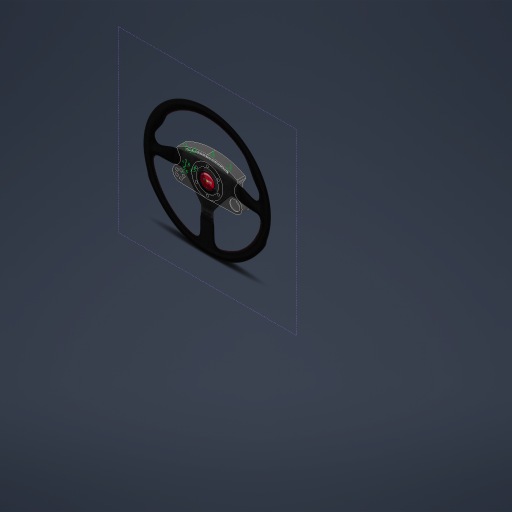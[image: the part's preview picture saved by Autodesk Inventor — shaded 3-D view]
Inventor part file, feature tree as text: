
AUTODESK INVENTOR PART (.ipt)
format: ipt  version: 2023 (Build 270158000, 158)  size: 2,766,848 bytes
history: native  units: mm
features: extrude x19, sketch x13, fillet x9, projected_geometry x6, other x3, chamfer x2, split x1, mirror x1, plane x1
ambient origin geometry x8: Origin, YZ Plane, XZ Plane, XY Plane, X Axis, Y Axis, Z Axis, Center Point
bodies: Solid1 (feature_tree)
feature tree (55):
  sketch  "Sketch1"  dims[d5=61.0mm d6=70.0mm]
  extrude  "Extrusion1"  Depth=70.0mm
  extrude  "Extrusion2"  Depth=60.0mm TaperAngle=360.0deg
  split  "Split1"
  sketch  "Sketch4"  dims[d14=86.0mm d36=20.0mm d37=0.0mm]
  sketch  "Sketch5"  dims[d38=40.0mm d49=75.888542mm]
  extrude  "Extrusion3"  Depth=20.0mm TaperAngle=0.0deg
  extrude  "Extrusion4"  Depth=75.888542mm
  extrude  "Extrusion5"  Depth=20.383104mm
  extrude  "Extrusion6"  Depth=28.0mm
  extrude  "Extrusion8"  Depth=10.458mm
  extrude  "Extrusion20"  Depth=50.0mm TaperAngle=360.0deg
  sketch  "Sketch7"  dims[d50=75.888542mm d51=20.383104mm]
  extrude  "Extrusion9"  Depth=10.0mm TaperAngle=360.0deg
  extrude  "Extrusion10"  Depth=13.5mm TaperAngle=0.0deg
  mirror  "Mirror1"
  extrude  "Extrusion11"  Depth=5.5mm
  extrude  "Extrusion12"  Depth=50.0mm TaperAngle=360.0deg
  chamfer  "Chamfer3"  Distance=13.5mm
  fillet  "Fillet1"  [1 undecoded]
  plane  "Work Plane4"
  sketch  "Sketch11"  dims[d54=1.5mm d55=0.0mm d61=10.458mm]
  sketch  "Sketch12"  dims[d62=8.0mm d63=50.0mm d65=360.0deg]
  extrude  "Extrusion14"  Depth=17.0mm
  extrude  "Extrusion19"  Depth=17.0mm
  extrude  "Extrusion15"  TaperAngle=90.0deg  [1 undecoded]
  fillet  "Fillet2"  Radius=2.0mm
  fillet  "Fillet3"  Radius=8.0mm
  extrude  "Extrusion16"  Depth=3.0mm TaperAngle=0.0deg
  sketch  "Sketch15"  dims[d77=5.0mm d78=0.0mm d82=5.5mm]
  extrude  "Extrusion17"  Depth=17.0mm
  extrude  "Extrusion18"  Depth=17.0mm
  fillet  "Fillet4"  Radius=3.5mm
  fillet  "Fillet5"  Radius=20.0mm
  fillet  "Fillet6"  Radius=20.0mm
  fillet  "Fillet7"  Radius=5.0mm
  fillet  "Fillet9"  Radius=5.0mm
  chamfer  "Chamfer6"  Distance=80.0mm
  sketch  "Sketch17"  dims[d83=1.0mm d84=50.0mm d86=360.0deg d88=13.5mm d89=0.0mm d92=0.0mm d93=0.0mm]
  fillet  "Fillet11"  Radius=2.0mm
  extrude  "Extrusion21"  Depth=17.0mm TaperAngle=45.0deg
  other  "Image1"
  other  "Image2"
  sketch  "Sketch2"  dims[d7=6.5mm d9=60.0mm d11=360.0deg]
  sketch  "Sketch8"  dims[d52=20.383104mm d53=28.0mm]
  sketch  "Sketch13"  dims[d67=10.0mm d68=50.0mm d70=360.0deg]
  sketch  "Sketch14"  dims[d72=0.0mm d73=0.0mm d74=13.5mm d75=0.0mm]
  projected_geometry  "Projected Loop4"
  projected_geometry  "Projected Loop5"
  projected_geometry  "Projected Loop6"
  projected_geometry  "Projected Loop7"
  projected_geometry  "Projected Loop8"
  projected_geometry  "Projected Loop9"
  other  "Image5"
  sketch  "Sketch18"  dims[d94=23.0mm d95=7.0mm d96=5.0mm d97=90.0deg d101=2.0mm d103=8.0mm d104=0.0mm d105=3.0mm d106=0.0mm d107=5.0mm d108=5.0mm d109=3.5mm d110=0.0mm d116=20.0mm d119=20.0mm d120=5.0mm d121=5.0mm d129=80.0mm d131=3.51199mm d148=2.0mm d149=0.0mm d154=1.5mm d155=2.0mm d156=45.0deg d164=7.0mm d165=1.0mm d166=50.0mm d168=360.0deg d170=0.0mm d242=1.0mm d243=1.0mm d244=1.0mm d245=1.0mm d246=1.0mm d247=1.0mm d248=1.0mm d249=1.0mm d250=1.0mm d251=1.0mm d252=1.0mm d253=1.0mm d254=1.0mm d255=1.0mm d256=1.0mm d257=1.0mm d258=1.0mm d259=1.0mm d260=1.0mm d261=1.0mm d262=1.0mm d263=1.0mm d264=1.0mm d265=1.0mm d266=1.0mm d267=1.0mm d268=1.0mm d269=1.0mm d270=1.0mm d271=1.0mm d272=1.0mm d273=1.0mm d274=1.0mm d275=1.0mm d276=1.0mm d277=1.0mm d278=1.0mm d279=1.0mm d280=1.0mm d281=1.0mm d282=1.0mm d283=1.0mm d284=1.0mm d285=1.0mm d286=1.0mm d287=1.0mm d288=1.0mm d289=1.0mm d290=1.0mm d291=1.0mm d292=1.0mm d293=1.0mm d294=1.0mm d295=1.0mm d296=1.0mm d297=1.0mm d298=1.0mm d299=1.0mm d300=1.0mm d301=1.0mm d302=1.0mm d303=1.0mm d304=1.0mm d305=1.0mm d306=1.0mm d307=1.0mm d308=1.0mm d309=1.0mm d310=1.0mm d311=1.0mm d312=1.0mm d313=1.0mm d314=1.0mm d315=1.0mm d316=1.0mm d317=1.0mm d318=1.0mm d319=1.0mm d320=1.0mm d321=1.0mm d322=1.0mm d323=1.0mm d324=1.0mm d325=1.0mm d326=1.0mm d327=1.0mm d328=1.0mm d329=1.0mm d330=1.0mm d331=1.0mm d332=1.0mm d333=1.0mm d334=1.0mm d335=1.0mm d336=1.0mm d337=1.0mm d338=1.0mm d339=1.0mm d340=1.0mm d341=1.0mm d342=1.0mm d343=1.0mm d344=1.0mm d345=1.0mm d348=10.5mm d349=0.0mm d350=5.0mm d351=8.061767mm d373=8.5mm d374=0.0mm d375=4.0mm d376=3.0mm d377=3.0mm d378=3.0mm d379=3.0mm d380=3.0mm d381=4.0mm d382=5.0mm d383=2.0mm d386=8.5mm d387=7.0mm d388=0.0mm d392=1.5mm d393=1.5mm d394=1.5mm d395=1.5mm d396=1.5mm d397=1.5mm d398=1.5mm d399=2.5mm d400=2.5mm d402=4.0mm d403=4.0mm d405=1.0mm d409=90.0deg d410=2.0mm d411=0.0mm d412=4.0mm d413=0.0mm d414=5.8mm d415=0.0mm d417=5.2mm d419=50.0mm d421=50.0mm d423=50.0mm d425=50.0mm d426=5.2mm d428=50.0mm d430=50.0mm d432=50.0mm d434=50.0mm d435=5.2mm d437=50.0mm d439=50.0mm d441=50.0mm d443=50.0mm d444=5.2mm d446=50.0mm d448=50.0mm d450=50.0mm d452=50.0mm d453=5.2mm d454=5.6mm d455=0.0mm d456=1.0mm d457=1.0mm d458=1.0mm d459=1.0mm d461=1.5mm d495=10.0mm d496=4.0mm d497=45.0deg d498=2.0mm d503=36.0mm d512=6.0mm d513=6.0mm d514=6.0mm d515=6.0mm d516=6.0mm d517=6.0mm d518=6.0mm d519=6.0mm d520=6.0mm d521=6.0mm d522=6.0mm d523=6.0mm d524=6.0mm d525=6.0mm d526=6.0mm d527=17.0mm d528=0.0mm d150=0.5mm d151=0.872665mm d152=0.5mm d153=0.872665mm d460=0.5mm d462=0.5mm d463=0.872665mm]
note: 2 required parameter values undecoded (feature->parameter linkage not recoverable at this tier; creation-order binding heuristic only, values carry confidence <= 0.55)
